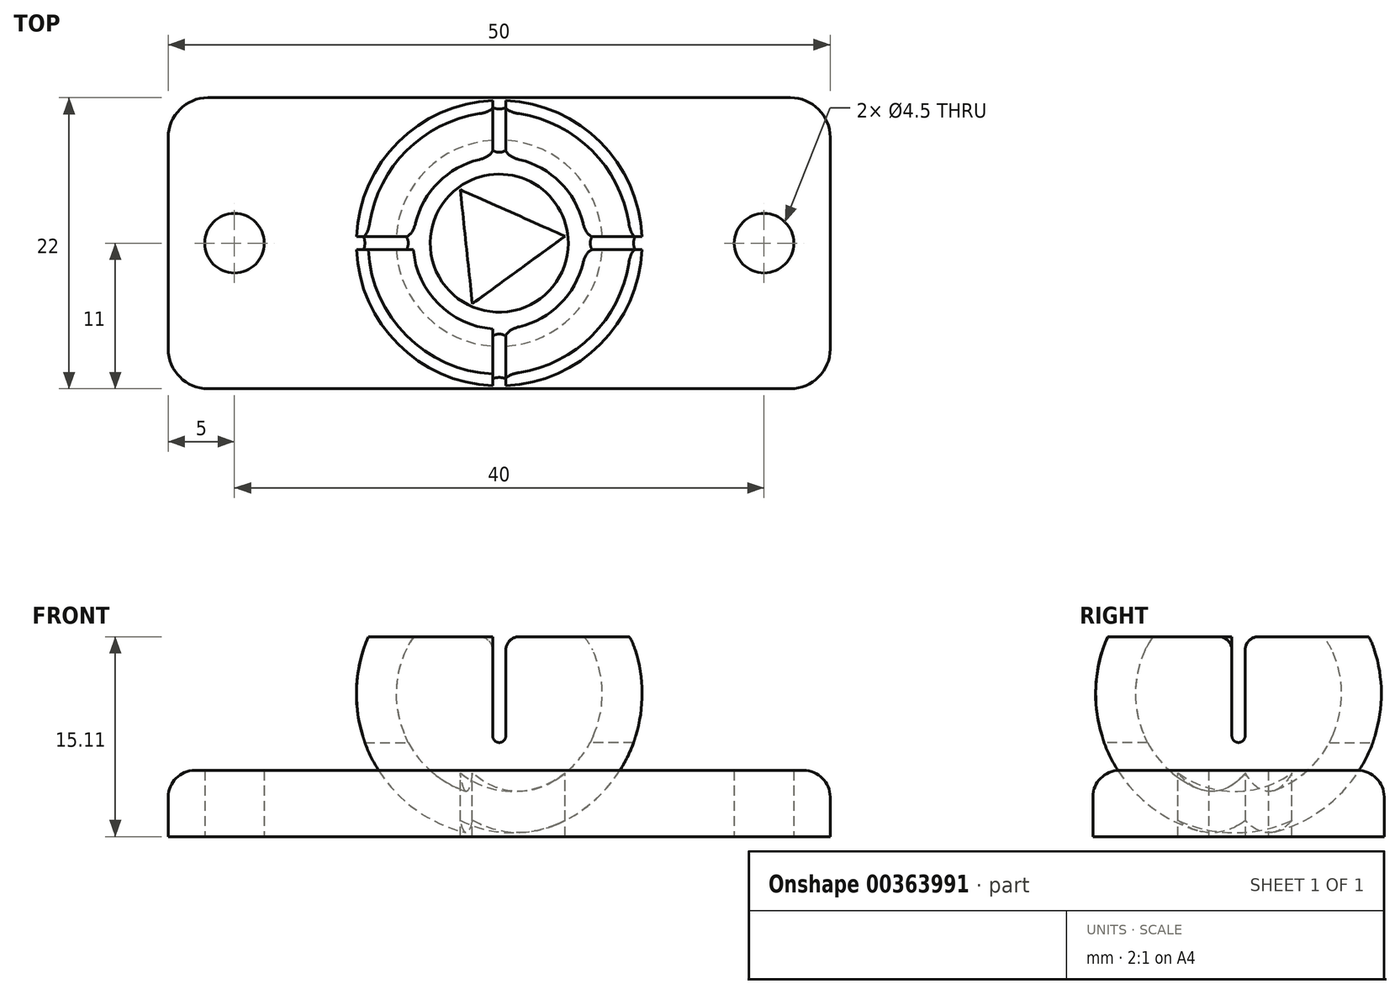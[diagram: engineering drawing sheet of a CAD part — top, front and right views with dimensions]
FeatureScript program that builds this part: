
annotation { "Feature Type Name" : "Feature", "Feature Type Description" : "" }
export const myFeature = defineFeature(function(context is Context, id is Id, definition is map)
    precondition{}
    {
        {
            var Q0;
            Q0=qCreatedBy(makeId("Front.planeOp"),FACE);
            var sketch = newSketch(context, id + "F0", { "sketchPlane" : qUnion([Q0])});
            skArc(sketch, "E0", {"start": v(0, -7.8) * mm, "mid": v(6.87, -3.69) * mm, "end": v(6.5, 4.31) * mm});
            skArc(sketch, "E1", {"start": v(0, -10.8) * mm, "mid": v(9.03, -5.92) * mm, "end": v(9.9, 4.31) * mm});
            skLineSegment(sketch, "E2", {"start": v(0, -7.8) * mm, "end": v(0, -10.8) * mm});
            skLineSegment(sketch, "E3", {"start": v(6.5, 4.31) * mm, "end": v(9.9, 4.31) * mm});
            skPoint(sketch, "E4.end.orphan", {"position": v(0, 10.8) * mm});
            skPoint(sketch, "E5.orphan", {"position": v(0, 7.8) * mm});
            skSolve(sketch);
        }
        {
            var Q0;
            Q0 = qSketchRegion(id + "F0", true);
            var Q1;
            Q1=sQuery(id+"F0.wireOp",EDGE,"E2");
            revolve(context, id + "F1", {"entities" : qUnion([Q0]), "axis" : qUnion([Q1]), "revolveType" : RevolveType.FULL});
        }
        {
            var Q0;
            Q0=sQuery(id+"F0.wireOp",VERTEX,"E2.end");
            var Q1;
            Q1=qCreatedBy(makeId("Top.planeOp"),FACE);
            cPlane(context, id + "F2", {"entities" : qUnion([Q0, Q1]), "cplaneType" : CPlaneType.PLANE_POINT, "offset" : 14.24 * mm, "oppositeDirection" : true, "width" : 150 * mm, "height" : 150 * mm});
        }
        {
            var Q0;
            Q0=qCreatedBy(id+"F2.planeOp",FACE);
            var sketch = newSketch(context, id + "F3", { "sketchPlane" : qUnion([Q0])});
            skLineSegment(sketch, "E6.bottom", {"start": v(-25, 11) * mm, "end": v(25, 11) * mm});
            skLineSegment(sketch, "E6.top", {"start": v(-25, -11) * mm, "end": v(25, -11) * mm});
            skLineSegment(sketch, "E6.left", {"start": v(-25, 11) * mm, "end": v(-25, -11) * mm});
            skLineSegment(sketch, "E6.right", {"start": v(25, 11) * mm, "end": v(25, -11) * mm});
            skCircle(sketch, "E7", {"center": v(-20, 0) * mm, "radius": 2.25 * mm});
            skCircle(sketch, "E8", {"center": v(20, 0) * mm, "radius": 2.25 * mm});
            skLineSegment(sketch, "E9", {"start": v(0, 11) * mm, "end": v(0, -11) * mm, "construction": true});
            skSolve(sketch);
        }
        {
            var Q0;
            Q0=makeQuery(id+"F3.imprint","IMPRINT",FACE,{"disambiguationData":[TD([[makeQuery(id+"F3.imprint","IMPRINT",EDGE,{"derivedFrom":sQuery(id+"F3.wireOp",EDGE,"E6.bottom")}),-1.0]])]});
            extrude(context, id + "F4", {"entities" : qUnion([Q0]), "depth" : 5 * mm});
        }
        {
            var Q0;
            Q0=qCreatedBy(makeId("Front.planeOp"),FACE);
            var sketch = newSketch(context, id + "F5", { "sketchPlane" : qUnion([Q0])});
            skArc(sketch, "E10", {"start": v(5.22, -5.8) * mm, "mid": v(2.8, -7.28) * mm, "end": v(0, -7.8) * mm});
            skLineSegment(sketch, "E11", {"start": v(0, -7.8) * mm, "end": v(0, -5.8) * mm});
            skLineSegment(sketch, "E12", {"start": v(0, -5.8) * mm, "end": v(5.22, -5.8) * mm});
            skSolve(sketch);
        }
        {
            var Q0;
            Q0 = qSketchRegion(id + "F5", true);
            var Q1;
            Q1=sQuery(id+"F5.wireOp",EDGE,"E11");
            revolve(context, id + "F6", {"operationType" : NewBodyOperationType.REMOVE, "entities" : qUnion([Q0]), "axis" : qUnion([Q1]), "revolveType" : RevolveType.FULL, "oppositeDirection" : true});
        }
        {
            var Q0;
            Q0=makeQuery(id+"F4.opExtrude","CAP_FACE",FACE,{"disambiguationData":[OSD([sQuery(id+"F3.wireOp",EDGE,"E6.bottom"),sQuery(id+"F3.wireOp",EDGE,"E6.top"),sQuery(id+"F3.wireOp",EDGE,"E6.left"),sQuery(id+"F3.wireOp",EDGE,"E6.right"),sQuery(id+"F3.wireOp",EDGE,"E7"),sQuery(id+"F3.wireOp",EDGE,"E8")])],"isStart":false});
            var sketch = newSketch(context, id + "F7", { "sketchPlane" : qUnion([Q0])});
            skCircle(sketch, "E13.cCircle", {"center": v(0, 0) * mm, "radius": 2.5 * mm, "construction": true});
            skLineSegment(sketch, "E13.0", {"start": v(-2.94, 4.04) * mm, "end": v(4.97, 0.53) * mm});
            skLineSegment(sketch, "E13.1", {"start": v(4.97, 0.53) * mm, "end": v(-2.03, -4.57) * mm});
            skLineSegment(sketch, "E13.2", {"start": v(-2.03, -4.57) * mm, "end": v(-2.94, 4.04) * mm});
            skPoint(sketch, "E13.0.midPoint", {"position": v(1.02, 2.28) * mm});
            skSolve(sketch);
        }
        {
            var Q0;
            Q0=makeQuery(id+"F7.imprint","IMPRINT",FACE,{"disambiguationData":[TD([[makeQuery(id+"F7.imprint","IMPRINT",EDGE,{"derivedFrom":sQuery(id+"F7.wireOp",EDGE,"E13.0")}),-1.0]])]});
            extrude(context, id + "F8", {"entities" : qUnion([Q0]), "operationType" : NewBodyOperationType.REMOVE, "endBound" : BoundingType.THROUGH_ALL, "oppositeDirection" : true, "depth" : 25 * mm});
        }
        {
            var Q0;
            Q0=makeQuery(id+"F1.opRevolve","SWEPT_FACE",FACE,{"disambiguationData":[OSD([sQuery(id+"F0.wireOp",EDGE,"E3")])]});
            var sketch = newSketch(context, id + "F9", { "sketchPlane" : qUnion([Q0])});
            skLineSegment(sketch, "E14.bottom", {"start": v(-0.5, 10.95) * mm, "end": v(0.5, 10.95) * mm});
            skLineSegment(sketch, "E14.top", {"start": v(-0.5, -11.42) * mm, "end": v(0.5, -11.42) * mm});
            skLineSegment(sketch, "E14.left", {"start": v(-0.5, 10.95) * mm, "end": v(-0.5, -11.42) * mm});
            skLineSegment(sketch, "E14.right", {"start": v(0.5, 10.95) * mm, "end": v(0.5, -11.42) * mm});
            skLineSegment(sketch, "E15.bottom", {"start": v(-12.67, 0.5) * mm, "end": v(11.36, 0.5) * mm});
            skLineSegment(sketch, "E15.top", {"start": v(-12.67, -0.5) * mm, "end": v(11.36, -0.5) * mm});
            skLineSegment(sketch, "E15.left", {"start": v(-12.67, 0.5) * mm, "end": v(-12.67, -0.5) * mm});
            skLineSegment(sketch, "E15.right", {"start": v(11.36, 0.5) * mm, "end": v(11.36, -0.5) * mm});
            skLineSegment(sketch, "E16", {"start": v(0, 13.57) * mm, "end": v(0, -13.22) * mm, "construction": true});
            skLineSegment(sketch, "E17", {"start": v(-14.62, 0) * mm, "end": v(19.57, 0) * mm, "construction": true});
            skSolve(sketch);
        }
        {
            var Q0;
            Q0 = qSketchRegion(id + "F9", true);
            extrude(context, id + "F10", {"entities" : qUnion([Q0]), "operationType" : NewBodyOperationType.REMOVE, "oppositeDirection" : true, "depth" : 8 * mm});
        }
        {
            var Q0;
            Q0=makeQuery(id+"F4.opExtrude","SWEPT_EDGE",EDGE,{"disambiguationData":[OSD([sQuery(id+"F3.wireOp",EDGE,"E6.top"),sQuery(id+"F3.wireOp",EDGE,"E6.left")])]});
            var Q1;
            Q1=makeQuery(id+"F4.opExtrude","SWEPT_EDGE",EDGE,{"disambiguationData":[OSD([sQuery(id+"F3.wireOp",EDGE,"E6.bottom"),sQuery(id+"F3.wireOp",EDGE,"E6.left")])]});
            var Q2;
            Q2=makeQuery(id+"F4.opExtrude","SWEPT_EDGE",EDGE,{"disambiguationData":[OSD([sQuery(id+"F3.wireOp",EDGE,"E6.bottom"),sQuery(id+"F3.wireOp",EDGE,"E6.right")])]});
            var Q3;
            Q3=makeQuery(id+"F4.opExtrude","SWEPT_EDGE",EDGE,{"disambiguationData":[OSD([sQuery(id+"F3.wireOp",EDGE,"E6.top"),sQuery(id+"F3.wireOp",EDGE,"E6.right")])]});
            fillet(context, id + "F11", {"entities" : qUnion([Q0, Q1, Q2, Q3]), "radius" : 3 * mm, "tangentPropagation" : true, "allowEdgeOverflow" : false});
        }
        {
            var Q0;
            {var subQ0=sQuery(id+"F9.wireOp",EDGE,"E15.bottom");var subQ1=sQuery(id+"F0.wireOp",EDGE,"E3");var subQ3=makeQuery(id+"F9.imprint","INTERSECT",VERTEX,{"disambiguationData":[OD(0.0)],"derivedFrom":[makeQuery(id+"F1.opRevolve","SWEPT_EDGE",EDGE,{"disambiguationData":[OSD([sQuery(id+"F0.wireOp",EDGE,"E1"),subQ1])]}),subQ0]});Q0=makeQuery(id+"F10.boolean.opBoolean","COPY",EDGE,{"derivedFrom":makeQuery(id+"F10.opExtrude","CAP_EDGE",EDGE,{"disambiguationData":[OSD([subQ0]),TDD([makeQuery(id+"F9.imprint","IMPRINT",EDGE,{"disambiguationData":[TD([[makeQuery(id+"F9.imprint","INTERSECT",VERTEX,{"derivedFrom":[subQ0,sQuery(id+"F9.wireOp",EDGE,"E15.left")]}),-1.0]])],"derivedFrom":subQ0}),makeQuery(id+"F9.imprint","IMPRINT",EDGE,{"disambiguationData":[TD([[subQ3,-1.0]])],"derivedFrom":subQ0}),makeQuery(id+"F9.imprint","IMPRINT",EDGE,{"disambiguationData":[TD([[makeQuery(id+"F9.imprint","INTERSECT",VERTEX,{"derivedFrom":[sQuery(id+"F9.wireOp",EDGE,"E14.left"),subQ0]}),1.0]])],"derivedFrom":subQ0})])],"isStart":true})});}
            var Q1;
            {var subQ0=sQuery(id+"F9.wireOp",EDGE,"E15.top");var subQ1=sQuery(id+"F0.wireOp",EDGE,"E3");var subQ3=makeQuery(id+"F9.imprint","INTERSECT",VERTEX,{"disambiguationData":[OD(0.0)],"derivedFrom":[makeQuery(id+"F1.opRevolve","SWEPT_EDGE",EDGE,{"disambiguationData":[OSD([sQuery(id+"F0.wireOp",EDGE,"E1"),subQ1])]}),subQ0]});Q1=makeQuery(id+"F10.boolean.opBoolean","COPY",EDGE,{"derivedFrom":makeQuery(id+"F10.opExtrude","CAP_EDGE",EDGE,{"disambiguationData":[OSD([subQ0]),TDD([makeQuery(id+"F9.imprint","IMPRINT",EDGE,{"disambiguationData":[TD([[makeQuery(id+"F9.imprint","INTERSECT",VERTEX,{"derivedFrom":[subQ0,sQuery(id+"F9.wireOp",EDGE,"E15.left")]}),-1.0]])],"derivedFrom":subQ0}),makeQuery(id+"F9.imprint","IMPRINT",EDGE,{"disambiguationData":[TD([[subQ3,-1.0]])],"derivedFrom":subQ0}),makeQuery(id+"F9.imprint","IMPRINT",EDGE,{"disambiguationData":[TD([[makeQuery(id+"F9.imprint","INTERSECT",VERTEX,{"derivedFrom":[sQuery(id+"F9.wireOp",EDGE,"E14.left"),subQ0]}),1.0]])],"derivedFrom":subQ0})])],"isStart":true})});}
            var Q2;
            {var subQ0=sQuery(id+"F9.wireOp",EDGE,"E14.left");var subQ1=sQuery(id+"F0.wireOp",EDGE,"E3");var subQ3=makeQuery(id+"F9.imprint","INTERSECT",VERTEX,{"disambiguationData":[OD(0.0)],"derivedFrom":[makeQuery(id+"F1.opRevolve","SWEPT_EDGE",EDGE,{"disambiguationData":[OSD([sQuery(id+"F0.wireOp",EDGE,"E1"),subQ1])]}),subQ0]});Q2=makeQuery(id+"F10.boolean.opBoolean","COPY",EDGE,{"derivedFrom":makeQuery(id+"F10.opExtrude","CAP_EDGE",EDGE,{"disambiguationData":[OSD([subQ0]),TDD([makeQuery(id+"F9.imprint","IMPRINT",EDGE,{"disambiguationData":[TD([[makeQuery(id+"F9.imprint","INTERSECT",VERTEX,{"derivedFrom":[sQuery(id+"F9.wireOp",EDGE,"E14.bottom"),subQ0]}),-1.0]])],"derivedFrom":subQ0}),makeQuery(id+"F9.imprint","IMPRINT",EDGE,{"disambiguationData":[TD([[subQ3,-1.0]])],"derivedFrom":subQ0}),makeQuery(id+"F9.imprint","IMPRINT",EDGE,{"disambiguationData":[TD([[makeQuery(id+"F9.imprint","INTERSECT",VERTEX,{"derivedFrom":[subQ0,sQuery(id+"F9.wireOp",EDGE,"E15.bottom")]}),1.0]])],"derivedFrom":subQ0})])],"isStart":true})});}
            var Q3;
            {var subQ0=sQuery(id+"F9.wireOp",EDGE,"E14.right");var subQ1=sQuery(id+"F0.wireOp",EDGE,"E3");var subQ3=makeQuery(id+"F9.imprint","INTERSECT",VERTEX,{"disambiguationData":[OD(0.0)],"derivedFrom":[makeQuery(id+"F1.opRevolve","SWEPT_EDGE",EDGE,{"disambiguationData":[OSD([sQuery(id+"F0.wireOp",EDGE,"E1"),subQ1])]}),subQ0]});Q3=makeQuery(id+"F10.boolean.opBoolean","COPY",EDGE,{"derivedFrom":makeQuery(id+"F10.opExtrude","CAP_EDGE",EDGE,{"disambiguationData":[OSD([subQ0]),TDD([makeQuery(id+"F9.imprint","IMPRINT",EDGE,{"disambiguationData":[TD([[makeQuery(id+"F9.imprint","INTERSECT",VERTEX,{"derivedFrom":[sQuery(id+"F9.wireOp",EDGE,"E14.bottom"),subQ0]}),-1.0]])],"derivedFrom":subQ0}),makeQuery(id+"F9.imprint","IMPRINT",EDGE,{"disambiguationData":[TD([[subQ3,-1.0]])],"derivedFrom":subQ0}),makeQuery(id+"F9.imprint","IMPRINT",EDGE,{"disambiguationData":[TD([[makeQuery(id+"F9.imprint","INTERSECT",VERTEX,{"derivedFrom":[subQ0,sQuery(id+"F9.wireOp",EDGE,"E15.bottom")]}),1.0]])],"derivedFrom":subQ0})])],"isStart":true})});}
            var Q4;
            {var subQ0=sQuery(id+"F9.wireOp",EDGE,"E15.bottom");var subQ1=sQuery(id+"F0.wireOp",EDGE,"E3");var subQ2=makeQuery(id+"F9.imprint","INTERSECT",VERTEX,{"disambiguationData":[OD(1.0)],"derivedFrom":[makeQuery(id+"F1.opRevolve","SWEPT_EDGE",EDGE,{"disambiguationData":[OSD([sQuery(id+"F0.wireOp",EDGE,"E1"),subQ1])]}),subQ0]});Q4=makeQuery(id+"F10.boolean.opBoolean","COPY",EDGE,{"derivedFrom":makeQuery(id+"F10.opExtrude","CAP_EDGE",EDGE,{"disambiguationData":[OSD([subQ0]),TDD([makeQuery(id+"F9.imprint","IMPRINT",EDGE,{"disambiguationData":[TD([[makeQuery(id+"F9.imprint","INTERSECT",VERTEX,{"derivedFrom":[sQuery(id+"F9.wireOp",EDGE,"E14.right"),subQ0]}),-1.0]])],"derivedFrom":subQ0}),makeQuery(id+"F9.imprint","IMPRINT",EDGE,{"disambiguationData":[TD([[subQ2,1.0]])],"derivedFrom":subQ0}),makeQuery(id+"F9.imprint","IMPRINT",EDGE,{"disambiguationData":[TD([[makeQuery(id+"F9.imprint","INTERSECT",VERTEX,{"derivedFrom":[subQ0,sQuery(id+"F9.wireOp",EDGE,"E15.right")]}),1.0]])],"derivedFrom":subQ0})])],"isStart":true})});}
            var Q5;
            {var subQ0=sQuery(id+"F9.wireOp",EDGE,"E15.top");var subQ1=sQuery(id+"F0.wireOp",EDGE,"E3");var subQ2=makeQuery(id+"F9.imprint","INTERSECT",VERTEX,{"disambiguationData":[OD(1.0)],"derivedFrom":[makeQuery(id+"F1.opRevolve","SWEPT_EDGE",EDGE,{"disambiguationData":[OSD([sQuery(id+"F0.wireOp",EDGE,"E1"),subQ1])]}),subQ0]});Q5=makeQuery(id+"F10.boolean.opBoolean","COPY",EDGE,{"derivedFrom":makeQuery(id+"F10.opExtrude","CAP_EDGE",EDGE,{"disambiguationData":[OSD([subQ0]),TDD([makeQuery(id+"F9.imprint","IMPRINT",EDGE,{"disambiguationData":[TD([[makeQuery(id+"F9.imprint","INTERSECT",VERTEX,{"derivedFrom":[sQuery(id+"F9.wireOp",EDGE,"E14.right"),subQ0]}),-1.0]])],"derivedFrom":subQ0}),makeQuery(id+"F9.imprint","IMPRINT",EDGE,{"disambiguationData":[TD([[subQ2,1.0]])],"derivedFrom":subQ0}),makeQuery(id+"F9.imprint","IMPRINT",EDGE,{"disambiguationData":[TD([[makeQuery(id+"F9.imprint","INTERSECT",VERTEX,{"derivedFrom":[subQ0,sQuery(id+"F9.wireOp",EDGE,"E15.right")]}),1.0]])],"derivedFrom":subQ0})])],"isStart":true})});}
            var Q6;
            {var subQ0=sQuery(id+"F9.wireOp",EDGE,"E14.right");var subQ1=sQuery(id+"F0.wireOp",EDGE,"E3");var subQ2=makeQuery(id+"F9.imprint","INTERSECT",VERTEX,{"disambiguationData":[OD(1.0)],"derivedFrom":[makeQuery(id+"F1.opRevolve","SWEPT_EDGE",EDGE,{"disambiguationData":[OSD([sQuery(id+"F0.wireOp",EDGE,"E1"),subQ1])]}),subQ0]});Q6=makeQuery(id+"F10.boolean.opBoolean","COPY",EDGE,{"derivedFrom":makeQuery(id+"F10.opExtrude","CAP_EDGE",EDGE,{"disambiguationData":[OSD([subQ0]),TDD([makeQuery(id+"F9.imprint","IMPRINT",EDGE,{"disambiguationData":[TD([[makeQuery(id+"F9.imprint","INTERSECT",VERTEX,{"derivedFrom":[subQ0,sQuery(id+"F9.wireOp",EDGE,"E15.top")]}),-1.0]])],"derivedFrom":subQ0}),makeQuery(id+"F9.imprint","IMPRINT",EDGE,{"disambiguationData":[TD([[subQ2,1.0]])],"derivedFrom":subQ0}),makeQuery(id+"F9.imprint","IMPRINT",EDGE,{"disambiguationData":[TD([[makeQuery(id+"F9.imprint","INTERSECT",VERTEX,{"derivedFrom":[sQuery(id+"F9.wireOp",EDGE,"E14.top"),subQ0]}),1.0]])],"derivedFrom":subQ0})])],"isStart":true})});}
            var Q7;
            {var subQ0=sQuery(id+"F9.wireOp",EDGE,"E14.left");var subQ1=sQuery(id+"F0.wireOp",EDGE,"E3");var subQ2=makeQuery(id+"F9.imprint","INTERSECT",VERTEX,{"disambiguationData":[OD(1.0)],"derivedFrom":[makeQuery(id+"F1.opRevolve","SWEPT_EDGE",EDGE,{"disambiguationData":[OSD([sQuery(id+"F0.wireOp",EDGE,"E1"),subQ1])]}),subQ0]});Q7=makeQuery(id+"F10.boolean.opBoolean","COPY",EDGE,{"derivedFrom":makeQuery(id+"F10.opExtrude","CAP_EDGE",EDGE,{"disambiguationData":[OSD([subQ0]),TDD([makeQuery(id+"F9.imprint","IMPRINT",EDGE,{"disambiguationData":[TD([[makeQuery(id+"F9.imprint","INTERSECT",VERTEX,{"derivedFrom":[subQ0,sQuery(id+"F9.wireOp",EDGE,"E15.top")]}),-1.0]])],"derivedFrom":subQ0}),makeQuery(id+"F9.imprint","IMPRINT",EDGE,{"disambiguationData":[TD([[subQ2,1.0]])],"derivedFrom":subQ0}),makeQuery(id+"F9.imprint","IMPRINT",EDGE,{"disambiguationData":[TD([[makeQuery(id+"F9.imprint","INTERSECT",VERTEX,{"derivedFrom":[sQuery(id+"F9.wireOp",EDGE,"E14.top"),subQ0]}),1.0]])],"derivedFrom":subQ0})])],"isStart":true})});}
            fillet(context, id + "F12", {"entities" : qUnion([Q0, Q1, Q2, Q3, Q4, Q5, Q6, Q7]), "radius" : 1 * mm, "tangentPropagation" : true, "allowEdgeOverflow" : false});
        }
        {
            var Q0;
            {var subQ0=sQuery(id+"F9.wireOp",EDGE,"E14.left");var subQ1=sQuery(id+"F0.wireOp",EDGE,"E3");var subQ2=makeQuery(id+"F9.imprint","INTERSECT",VERTEX,{"disambiguationData":[OD(1.0)],"derivedFrom":[makeQuery(id+"F1.opRevolve","SWEPT_EDGE",EDGE,{"disambiguationData":[OSD([sQuery(id+"F0.wireOp",EDGE,"E1"),subQ1])]}),subQ0]});Q0=makeQuery(id+"F10.boolean.opBoolean","COPY",EDGE,{"derivedFrom":makeQuery(id+"F10.opExtrude","CAP_EDGE",EDGE,{"disambiguationData":[OSD([subQ0]),TDD([makeQuery(id+"F9.imprint","IMPRINT",EDGE,{"disambiguationData":[TD([[makeQuery(id+"F9.imprint","INTERSECT",VERTEX,{"derivedFrom":[subQ0,sQuery(id+"F9.wireOp",EDGE,"E15.top")]}),-1.0]])],"derivedFrom":subQ0}),makeQuery(id+"F9.imprint","IMPRINT",EDGE,{"disambiguationData":[TD([[subQ2,1.0]])],"derivedFrom":subQ0}),makeQuery(id+"F9.imprint","IMPRINT",EDGE,{"disambiguationData":[TD([[makeQuery(id+"F9.imprint","INTERSECT",VERTEX,{"derivedFrom":[sQuery(id+"F9.wireOp",EDGE,"E14.top"),subQ0]}),1.0]])],"derivedFrom":subQ0})])],"isStart":false})});}
            var Q1;
            {var subQ0=sQuery(id+"F9.wireOp",EDGE,"E14.right");var subQ1=sQuery(id+"F0.wireOp",EDGE,"E3");var subQ2=makeQuery(id+"F9.imprint","INTERSECT",VERTEX,{"disambiguationData":[OD(1.0)],"derivedFrom":[makeQuery(id+"F1.opRevolve","SWEPT_EDGE",EDGE,{"disambiguationData":[OSD([sQuery(id+"F0.wireOp",EDGE,"E1"),subQ1])]}),subQ0]});Q1=makeQuery(id+"F10.boolean.opBoolean","COPY",EDGE,{"derivedFrom":makeQuery(id+"F10.opExtrude","CAP_EDGE",EDGE,{"disambiguationData":[OSD([subQ0]),TDD([makeQuery(id+"F9.imprint","IMPRINT",EDGE,{"disambiguationData":[TD([[makeQuery(id+"F9.imprint","INTERSECT",VERTEX,{"derivedFrom":[subQ0,sQuery(id+"F9.wireOp",EDGE,"E15.top")]}),-1.0]])],"derivedFrom":subQ0}),makeQuery(id+"F9.imprint","IMPRINT",EDGE,{"disambiguationData":[TD([[subQ2,1.0]])],"derivedFrom":subQ0}),makeQuery(id+"F9.imprint","IMPRINT",EDGE,{"disambiguationData":[TD([[makeQuery(id+"F9.imprint","INTERSECT",VERTEX,{"derivedFrom":[sQuery(id+"F9.wireOp",EDGE,"E14.top"),subQ0]}),1.0]])],"derivedFrom":subQ0})])],"isStart":false})});}
            var Q2;
            {var subQ0=sQuery(id+"F9.wireOp",EDGE,"E15.bottom");var subQ1=sQuery(id+"F0.wireOp",EDGE,"E3");var subQ2=makeQuery(id+"F9.imprint","INTERSECT",VERTEX,{"disambiguationData":[OD(1.0)],"derivedFrom":[makeQuery(id+"F1.opRevolve","SWEPT_EDGE",EDGE,{"disambiguationData":[OSD([sQuery(id+"F0.wireOp",EDGE,"E1"),subQ1])]}),subQ0]});Q2=makeQuery(id+"F10.boolean.opBoolean","COPY",EDGE,{"derivedFrom":makeQuery(id+"F10.opExtrude","CAP_EDGE",EDGE,{"disambiguationData":[OSD([subQ0]),TDD([makeQuery(id+"F9.imprint","IMPRINT",EDGE,{"disambiguationData":[TD([[makeQuery(id+"F9.imprint","INTERSECT",VERTEX,{"derivedFrom":[sQuery(id+"F9.wireOp",EDGE,"E14.right"),subQ0]}),-1.0]])],"derivedFrom":subQ0}),makeQuery(id+"F9.imprint","IMPRINT",EDGE,{"disambiguationData":[TD([[subQ2,1.0]])],"derivedFrom":subQ0}),makeQuery(id+"F9.imprint","IMPRINT",EDGE,{"disambiguationData":[TD([[makeQuery(id+"F9.imprint","INTERSECT",VERTEX,{"derivedFrom":[subQ0,sQuery(id+"F9.wireOp",EDGE,"E15.right")]}),1.0]])],"derivedFrom":subQ0})])],"isStart":false})});}
            var Q3;
            {var subQ0=sQuery(id+"F9.wireOp",EDGE,"E15.top");var subQ1=sQuery(id+"F0.wireOp",EDGE,"E3");var subQ2=makeQuery(id+"F9.imprint","INTERSECT",VERTEX,{"disambiguationData":[OD(1.0)],"derivedFrom":[makeQuery(id+"F1.opRevolve","SWEPT_EDGE",EDGE,{"disambiguationData":[OSD([sQuery(id+"F0.wireOp",EDGE,"E1"),subQ1])]}),subQ0]});Q3=makeQuery(id+"F10.boolean.opBoolean","COPY",EDGE,{"derivedFrom":makeQuery(id+"F10.opExtrude","CAP_EDGE",EDGE,{"disambiguationData":[OSD([subQ0]),TDD([makeQuery(id+"F9.imprint","IMPRINT",EDGE,{"disambiguationData":[TD([[makeQuery(id+"F9.imprint","INTERSECT",VERTEX,{"derivedFrom":[sQuery(id+"F9.wireOp",EDGE,"E14.right"),subQ0]}),-1.0]])],"derivedFrom":subQ0}),makeQuery(id+"F9.imprint","IMPRINT",EDGE,{"disambiguationData":[TD([[subQ2,1.0]])],"derivedFrom":subQ0}),makeQuery(id+"F9.imprint","IMPRINT",EDGE,{"disambiguationData":[TD([[makeQuery(id+"F9.imprint","INTERSECT",VERTEX,{"derivedFrom":[subQ0,sQuery(id+"F9.wireOp",EDGE,"E15.right")]}),1.0]])],"derivedFrom":subQ0})])],"isStart":false})});}
            var Q4;
            {var subQ0=sQuery(id+"F9.wireOp",EDGE,"E14.right");var subQ1=sQuery(id+"F0.wireOp",EDGE,"E3");var subQ3=makeQuery(id+"F9.imprint","INTERSECT",VERTEX,{"disambiguationData":[OD(0.0)],"derivedFrom":[makeQuery(id+"F1.opRevolve","SWEPT_EDGE",EDGE,{"disambiguationData":[OSD([sQuery(id+"F0.wireOp",EDGE,"E1"),subQ1])]}),subQ0]});Q4=makeQuery(id+"F10.boolean.opBoolean","COPY",EDGE,{"derivedFrom":makeQuery(id+"F10.opExtrude","CAP_EDGE",EDGE,{"disambiguationData":[OSD([subQ0]),TDD([makeQuery(id+"F9.imprint","IMPRINT",EDGE,{"disambiguationData":[TD([[makeQuery(id+"F9.imprint","INTERSECT",VERTEX,{"derivedFrom":[sQuery(id+"F9.wireOp",EDGE,"E14.bottom"),subQ0]}),-1.0]])],"derivedFrom":subQ0}),makeQuery(id+"F9.imprint","IMPRINT",EDGE,{"disambiguationData":[TD([[subQ3,-1.0]])],"derivedFrom":subQ0}),makeQuery(id+"F9.imprint","IMPRINT",EDGE,{"disambiguationData":[TD([[makeQuery(id+"F9.imprint","INTERSECT",VERTEX,{"derivedFrom":[subQ0,sQuery(id+"F9.wireOp",EDGE,"E15.bottom")]}),1.0]])],"derivedFrom":subQ0})])],"isStart":false})});}
            var Q5;
            {var subQ0=sQuery(id+"F9.wireOp",EDGE,"E14.left");var subQ1=sQuery(id+"F0.wireOp",EDGE,"E3");var subQ3=makeQuery(id+"F9.imprint","INTERSECT",VERTEX,{"disambiguationData":[OD(0.0)],"derivedFrom":[makeQuery(id+"F1.opRevolve","SWEPT_EDGE",EDGE,{"disambiguationData":[OSD([sQuery(id+"F0.wireOp",EDGE,"E1"),subQ1])]}),subQ0]});Q5=makeQuery(id+"F10.boolean.opBoolean","COPY",EDGE,{"derivedFrom":makeQuery(id+"F10.opExtrude","CAP_EDGE",EDGE,{"disambiguationData":[OSD([subQ0]),TDD([makeQuery(id+"F9.imprint","IMPRINT",EDGE,{"disambiguationData":[TD([[makeQuery(id+"F9.imprint","INTERSECT",VERTEX,{"derivedFrom":[sQuery(id+"F9.wireOp",EDGE,"E14.bottom"),subQ0]}),-1.0]])],"derivedFrom":subQ0}),makeQuery(id+"F9.imprint","IMPRINT",EDGE,{"disambiguationData":[TD([[subQ3,-1.0]])],"derivedFrom":subQ0}),makeQuery(id+"F9.imprint","IMPRINT",EDGE,{"disambiguationData":[TD([[makeQuery(id+"F9.imprint","INTERSECT",VERTEX,{"derivedFrom":[subQ0,sQuery(id+"F9.wireOp",EDGE,"E15.bottom")]}),1.0]])],"derivedFrom":subQ0})])],"isStart":false})});}
            var Q6;
            {var subQ0=sQuery(id+"F9.wireOp",EDGE,"E15.top");var subQ1=sQuery(id+"F0.wireOp",EDGE,"E3");var subQ3=makeQuery(id+"F9.imprint","INTERSECT",VERTEX,{"disambiguationData":[OD(0.0)],"derivedFrom":[makeQuery(id+"F1.opRevolve","SWEPT_EDGE",EDGE,{"disambiguationData":[OSD([sQuery(id+"F0.wireOp",EDGE,"E1"),subQ1])]}),subQ0]});Q6=makeQuery(id+"F10.boolean.opBoolean","COPY",EDGE,{"derivedFrom":makeQuery(id+"F10.opExtrude","CAP_EDGE",EDGE,{"disambiguationData":[OSD([subQ0]),TDD([makeQuery(id+"F9.imprint","IMPRINT",EDGE,{"disambiguationData":[TD([[makeQuery(id+"F9.imprint","INTERSECT",VERTEX,{"derivedFrom":[subQ0,sQuery(id+"F9.wireOp",EDGE,"E15.left")]}),-1.0]])],"derivedFrom":subQ0}),makeQuery(id+"F9.imprint","IMPRINT",EDGE,{"disambiguationData":[TD([[subQ3,-1.0]])],"derivedFrom":subQ0}),makeQuery(id+"F9.imprint","IMPRINT",EDGE,{"disambiguationData":[TD([[makeQuery(id+"F9.imprint","INTERSECT",VERTEX,{"derivedFrom":[sQuery(id+"F9.wireOp",EDGE,"E14.left"),subQ0]}),1.0]])],"derivedFrom":subQ0})])],"isStart":false})});}
            var Q7;
            {var subQ0=sQuery(id+"F9.wireOp",EDGE,"E15.bottom");var subQ1=sQuery(id+"F0.wireOp",EDGE,"E3");var subQ3=makeQuery(id+"F9.imprint","INTERSECT",VERTEX,{"disambiguationData":[OD(0.0)],"derivedFrom":[makeQuery(id+"F1.opRevolve","SWEPT_EDGE",EDGE,{"disambiguationData":[OSD([sQuery(id+"F0.wireOp",EDGE,"E1"),subQ1])]}),subQ0]});Q7=makeQuery(id+"F10.boolean.opBoolean","COPY",EDGE,{"derivedFrom":makeQuery(id+"F10.opExtrude","CAP_EDGE",EDGE,{"disambiguationData":[OSD([subQ0]),TDD([makeQuery(id+"F9.imprint","IMPRINT",EDGE,{"disambiguationData":[TD([[makeQuery(id+"F9.imprint","INTERSECT",VERTEX,{"derivedFrom":[subQ0,sQuery(id+"F9.wireOp",EDGE,"E15.left")]}),-1.0]])],"derivedFrom":subQ0}),makeQuery(id+"F9.imprint","IMPRINT",EDGE,{"disambiguationData":[TD([[subQ3,-1.0]])],"derivedFrom":subQ0}),makeQuery(id+"F9.imprint","IMPRINT",EDGE,{"disambiguationData":[TD([[makeQuery(id+"F9.imprint","INTERSECT",VERTEX,{"derivedFrom":[sQuery(id+"F9.wireOp",EDGE,"E14.left"),subQ0]}),1.0]])],"derivedFrom":subQ0})])],"isStart":false})});}
            fillet(context, id + "F13", {"entities" : qUnion([Q0, Q1, Q2, Q3, Q4, Q5, Q6, Q7]), "radius" : 0.5 * mm, "tangentPropagation" : true, "allowEdgeOverflow" : false});
        }
        {
            var Q0;
            Q0=makeQuery(id+"F4.opExtrude","CAP_EDGE",EDGE,{"disambiguationData":[OSD([sQuery(id+"F3.wireOp",EDGE,"E6.right")])],"isStart":false});
            fillet(context, id + "F14", {"entities" : qUnion([Q0]), "radius" : 2 * mm, "tangentPropagation" : true, "allowEdgeOverflow" : false});
        }
    });
